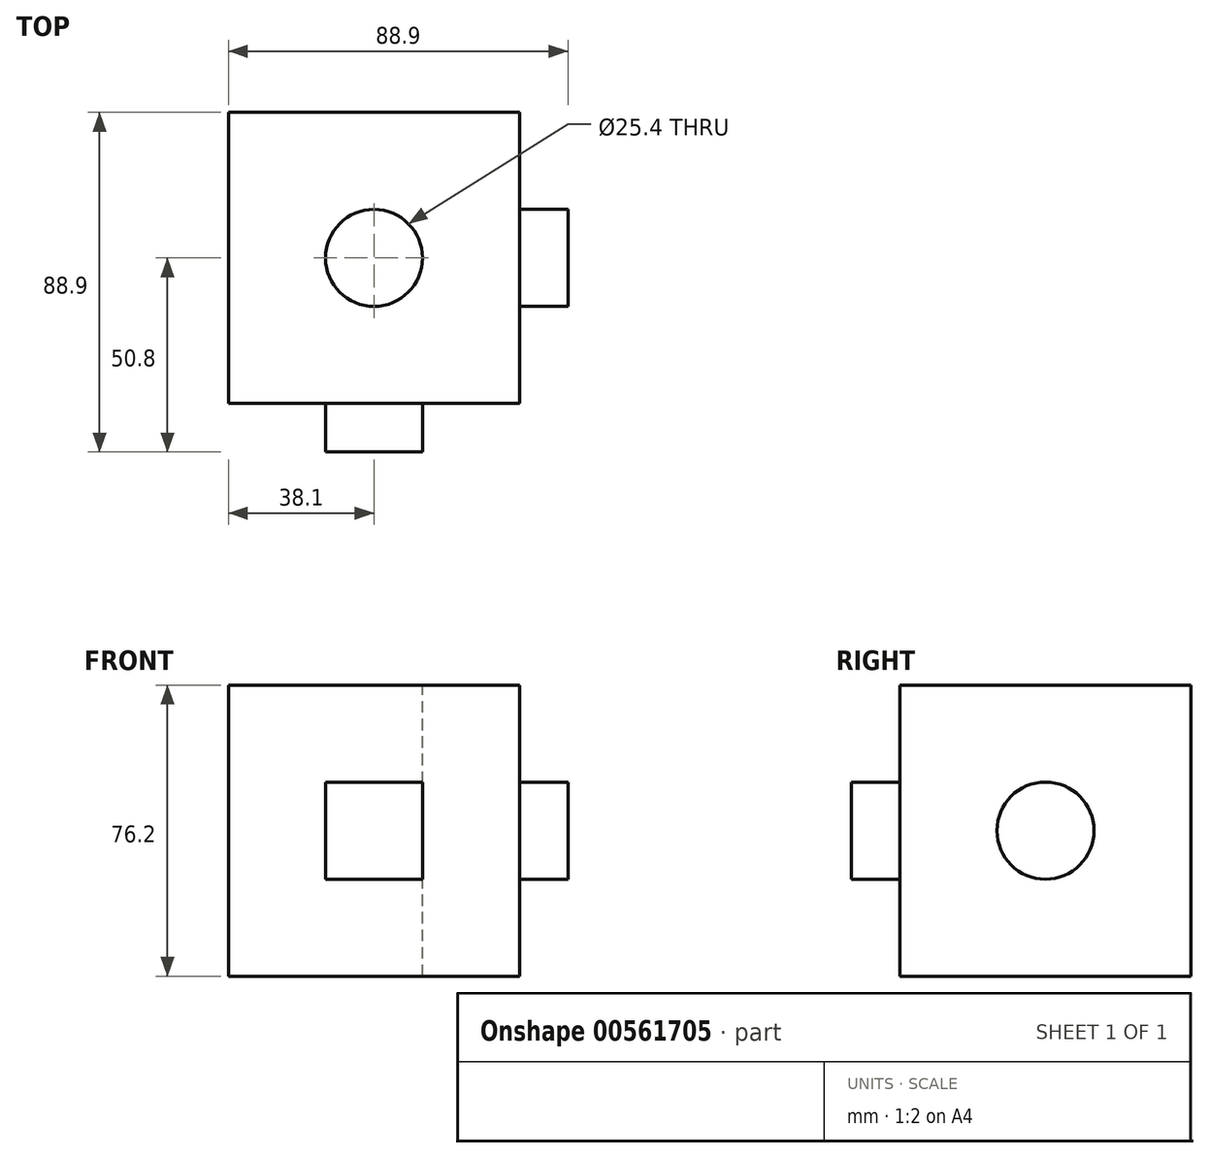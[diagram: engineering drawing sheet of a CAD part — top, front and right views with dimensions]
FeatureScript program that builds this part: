
annotation { "Feature Type Name" : "Feature", "Feature Type Description" : "" }
export const myFeature = defineFeature(function(context is Context, id is Id, definition is map)
    precondition{}
    {
        {
            var Q0;
            Q0=qCreatedBy(makeId("Front.planeOp"),FACE);
            var sketch = newSketch(context, id + "F0", { "sketchPlane" : qUnion([Q0])});
            skLineSegment(sketch, "E0.bottom", {"start": v(0, 0) * mm, "end": v(76.2, 0) * mm});
            skLineSegment(sketch, "E0.top", {"start": v(0, 76.2) * mm, "end": v(76.2, 76.2) * mm});
            skLineSegment(sketch, "E0.left", {"start": v(0, 0) * mm, "end": v(0, 76.2) * mm});
            skLineSegment(sketch, "E0.right", {"start": v(76.2, 0) * mm, "end": v(76.2, 76.2) * mm});
            skSolve(sketch);
        }
        {
            var Q0;
            Q0=makeQuery(id+"F0.imprint","IMPRINT",FACE,{"disambiguationData":[TD([[makeQuery(id+"F0.imprint","IMPRINT",EDGE,{"derivedFrom":sQuery(id+"F0.wireOp",EDGE,"E0.bottom")}),1.0]])]});
            extrude(context, id + "F1", {"entities" : qUnion([Q0]), "depth" : 76.2 * mm, "offsetDistance" : 25.4 * mm});
        }
        {
            var Q0;
            Q0=makeQuery(id+"F1.opExtrude","SWEPT_FACE",FACE,{"disambiguationData":[OSD([sQuery(id+"F0.wireOp",EDGE,"E0.top")])]});
            var sketch = newSketch(context, id + "F2", { "sketchPlane" : qUnion([Q0])});
            skPoint(sketch, "E1", {"position": v(38.1, -38.1) * mm});
            skSolve(sketch);
        }
        {
            var Q0;
            Q0=sQuery(id+"F2.wireOp",VERTEX,"E1");
            var Q1;
            Q1=makeQuery(id+"F1.opExtrude","SWEPT_BODY",BODY,{"disambiguationData":[OSD([sQuery(id+"F0.wireOp",EDGE,"E0.bottom"),sQuery(id+"F0.wireOp",EDGE,"E0.top"),sQuery(id+"F0.wireOp",EDGE,"E0.left"),sQuery(id+"F0.wireOp",EDGE,"E0.right")])]});
            hole(context, id + "F3", {"style" : HoleStyle.SIMPLE, "endStyle" : HoleEndStyle.THROUGH, "holeDiameter" : 25.4 * mm, "isTappedThrough" : true, "tappedDepth" : 12.7 * mm, "tapClearance" : 3, "locations" : qUnion([Q0]), "scope" : qUnion([Q1])});
        }
        {
            var Q0;
            Q0=makeQuery(id+"F1.opExtrude","CAP_FACE",FACE,{"disambiguationData":[OSD([sQuery(id+"F0.wireOp",EDGE,"E0.bottom"),sQuery(id+"F0.wireOp",EDGE,"E0.top"),sQuery(id+"F0.wireOp",EDGE,"E0.left"),sQuery(id+"F0.wireOp",EDGE,"E0.right")])],"isStart":false});
            var sketch = newSketch(context, id + "F4", { "sketchPlane" : qUnion([Q0])});
            skLineSegment(sketch, "E2.bottom", {"start": v(25.4, 50.8) * mm, "end": v(50.8, 50.8) * mm});
            skLineSegment(sketch, "E2.top", {"start": v(25.4, 25.4) * mm, "end": v(50.8, 25.4) * mm});
            skLineSegment(sketch, "E2.left", {"start": v(25.4, 50.8) * mm, "end": v(25.4, 25.4) * mm});
            skLineSegment(sketch, "E2.right", {"start": v(50.8, 50.8) * mm, "end": v(50.8, 25.4) * mm});
            skSolve(sketch);
        }
        {
            var Q0;
            Q0=makeQuery(id+"F4.imprint","IMPRINT",FACE,{"disambiguationData":[TD([[makeQuery(id+"F4.imprint","IMPRINT",EDGE,{"derivedFrom":sQuery(id+"F4.wireOp",EDGE,"E2.bottom")}),-1.0]])]});
            extrude(context, id + "F5", {"entities" : qUnion([Q0]), "operationType" : NewBodyOperationType.ADD, "depth" : 12.7 * mm, "offsetDistance" : 25.4 * mm});
        }
        {
            var Q0;
            Q0=makeQuery(id+"F1.opExtrude","SWEPT_FACE",FACE,{"disambiguationData":[OSD([sQuery(id+"F0.wireOp",EDGE,"E0.right")])]});
            var sketch = newSketch(context, id + "F6", { "sketchPlane" : qUnion([Q0])});
            skPoint(sketch, "E3", {"position": v(-38.1, 38.1) * mm});
            skCircle(sketch, "E4", {"center": v(-38.1, 38.1) * mm, "radius": 12.7 * mm});
            skSolve(sketch);
        }
        {
            var Q0;
            Q0=makeQuery(id+"F6.imprint","IMPRINT",FACE,{"disambiguationData":[TD([[makeQuery(id+"F6.imprint","IMPRINT",EDGE,{"derivedFrom":sQuery(id+"F6.wireOp",EDGE,"E4")}),1.0]])]});
            extrude(context, id + "F7", {"entities" : qUnion([Q0]), "operationType" : NewBodyOperationType.ADD, "depth" : 12.7 * mm, "offsetDistance" : 25.4 * mm});
        }
    });
